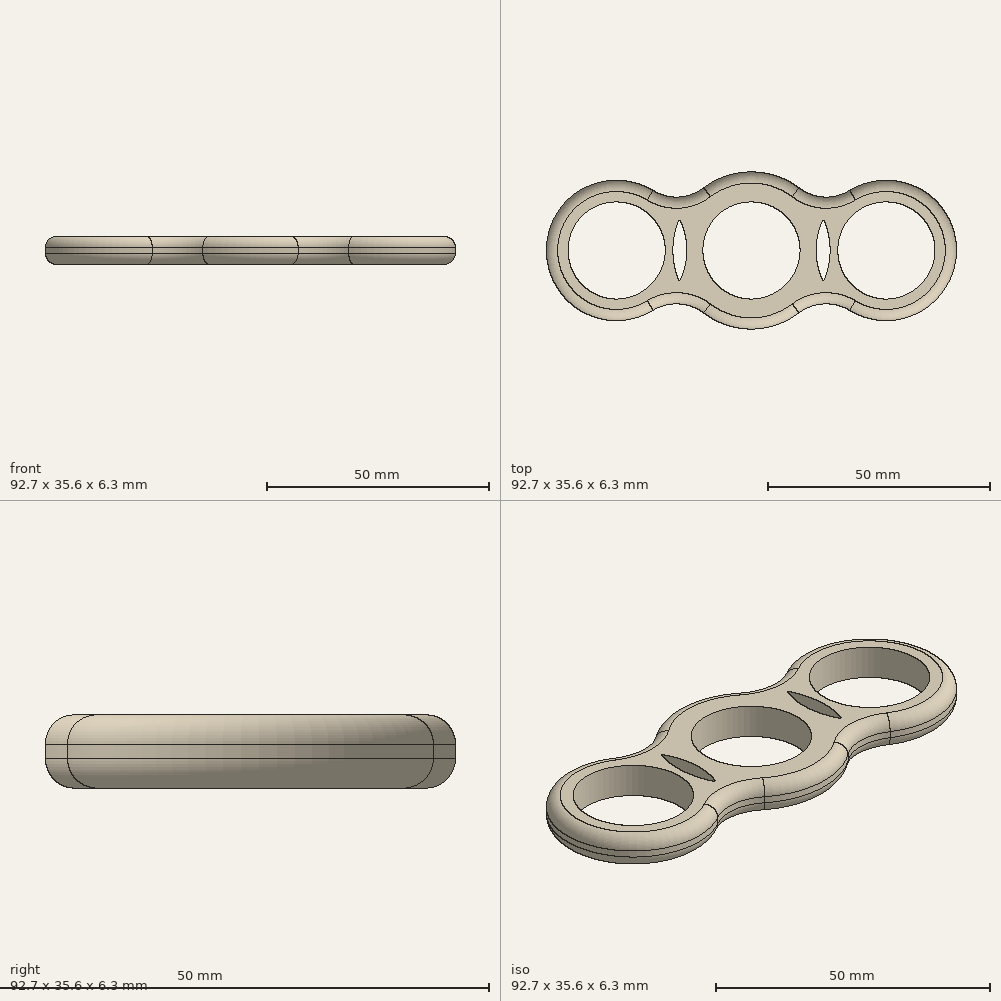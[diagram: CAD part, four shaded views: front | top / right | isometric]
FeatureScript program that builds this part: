
annotation { "Feature Type Name" : "Feature", "Feature Type Description" : "" }
export const myFeature = defineFeature(function(context is Context, id is Id, definition is map)
    precondition{}
    {
        {
            var Q0;
            Q0=qCreatedBy(makeId("Top.planeOp"),FACE);
            var sketch = newSketch(context, id + "F0", { "sketchPlane" : qUnion([Q0])});
            skCircle(sketch, "E0", {"center": v(0, 0) * mm, "radius": 10.99 * mm});
            skLineSegment(sketch, "E1", {"start": v(0, 0) * mm, "end": v(30.48, 0) * mm});
            skLineSegment(sketch, "E2", {"start": v(0, 0) * mm, "end": v(-30.48, 0) * mm});
            skCircle(sketch, "E3", {"center": v(-30.48, 0) * mm, "radius": 10.99 * mm});
            skCircle(sketch, "E4", {"center": v(30.48, 0) * mm, "radius": 10.99 * mm});
            skCircle(sketch, "E5", {"center": v(-30.48, 0) * mm, "radius": 15.88 * mm});
            skCircle(sketch, "E6", {"center": v(30.48, 0) * mm, "radius": 15.88 * mm});
            skCircle(sketch, "E7", {"center": v(0, 0) * mm, "radius": 17.78 * mm});
            skArc(sketch, "E8", {"start": v(-22.22, 13.55) * mm, "mid": v(-16.4, 12.08) * mm, "end": v(-10.77, 14.15) * mm});
            skArc(sketch, "E9", {"start": v(-10.77, -14.15) * mm, "mid": v(-16.4, -12.08) * mm, "end": v(-22.22, -13.55) * mm});
            skArc(sketch, "E10", {"start": v(10.77, 14.15) * mm, "mid": v(16.4, 12.08) * mm, "end": v(22.22, 13.55) * mm});
            skArc(sketch, "E11", {"start": v(22.22, -13.55) * mm, "mid": v(16.4, -12.08) * mm, "end": v(10.77, -14.15) * mm});
            skSolve(sketch);
        }
        {
            var Q0;
            Q0=makeQuery(id+"F0.imprint","IMPRINT",FACE,{"disambiguationData":[TD([[makeQuery(id+"F0.imprint","IMPRINT",EDGE,{"derivedFrom":sQuery(id+"F0.wireOp",EDGE,"E3")}),-1.0]])]});
            var Q1;
            {var subQ0=sQuery(id+"F0.wireOp",EDGE,"E8");Q1=makeQuery(id+"F0.imprint","IMPRINT",FACE,{"disambiguationData":[TD([[makeQuery(id+"F0.imprint","IMPRINT",EDGE,{"derivedFrom":subQ0}),-1.0]])]});}
            var Q2;
            {var subQ0=sQuery(id+"F0.wireOp",EDGE,"E9");Q2=makeQuery(id+"F0.imprint","IMPRINT",FACE,{"disambiguationData":[TD([[makeQuery(id+"F0.imprint","IMPRINT",EDGE,{"derivedFrom":subQ0}),-1.0]])]});}
            var Q3;
            {var subQ5=sQuery(id+"F0.wireOp",EDGE,"E1");var subQ6=sQuery(id+"F0.wireOp",EDGE,"E0");var subQ7=makeQuery(id+"F0.imprint","INTERSECT",VERTEX,{"derivedFrom":[subQ6,subQ5]});Q3=makeQuery(id+"F0.imprint","IMPRINT",FACE,{"disambiguationData":[TD([[makeQuery(id+"F0.imprint","IMPRINT",EDGE,{"disambiguationData":[TD([[subQ7,1.0]])],"derivedFrom":subQ6}),-1.0]])]});}
            var Q4;
            {var subQ5=sQuery(id+"F0.wireOp",EDGE,"E1");var subQ6=sQuery(id+"F0.wireOp",EDGE,"E0");var subQ7=makeQuery(id+"F0.imprint","INTERSECT",VERTEX,{"derivedFrom":[subQ6,subQ5]});Q4=makeQuery(id+"F0.imprint","IMPRINT",FACE,{"disambiguationData":[TD([[makeQuery(id+"F0.imprint","IMPRINT",EDGE,{"disambiguationData":[TD([[subQ7,-1.0]])],"derivedFrom":subQ6}),-1.0]])]});}
            var Q5;
            {var subQ0=sQuery(id+"F0.wireOp",EDGE,"E10");var subQ1=sQuery(id+"F0.wireOp",EDGE,"E6");var subQ2=makeQuery(id+"F0.imprint","INTERSECT",VERTEX,{"derivedFrom":[subQ1,subQ0]});Q5=makeQuery(id+"F0.imprint","IMPRINT",FACE,{"disambiguationData":[TD([[makeQuery(id+"F0.imprint","IMPRINT",EDGE,{"disambiguationData":[TD([[subQ2,-1.0]])],"derivedFrom":subQ1}),-1.0]])]});}
            var Q6;
            {var subQ0=sQuery(id+"F0.wireOp",EDGE,"E11");Q6=makeQuery(id+"F0.imprint","IMPRINT",FACE,{"disambiguationData":[TD([[makeQuery(id+"F0.imprint","IMPRINT",EDGE,{"derivedFrom":subQ0}),-1.0]])]});}
            var Q7;
            Q7=makeQuery(id+"F0.imprint","IMPRINT",FACE,{"disambiguationData":[TD([[makeQuery(id+"F0.imprint","IMPRINT",EDGE,{"derivedFrom":sQuery(id+"F0.wireOp",EDGE,"E4")}),-1.0]])]});
            extrude(context, id + "F1", {"entities" : qUnion([Q0, Q1, Q2, Q3, Q4, Q5, Q6, Q7]), "depth" : 6.35 * mm, "offsetDistance" : 25.4 * mm});
        }
        {
            var Q0;
            {var subQ0=sQuery(id+"F0.wireOp",EDGE,"E5");Q0=makeQuery(id+"F1.opExtrude","CAP_EDGE",EDGE,{"disambiguationData":[OSD([subQ0]),TDD([makeQuery(id+"F0.imprint","IMPRINT",EDGE,{"disambiguationData":[TD([[makeQuery(id+"F0.imprint","INTERSECT",VERTEX,{"derivedFrom":[subQ0,sQuery(id+"F0.wireOp",EDGE,"E8")]}),-1.0]])],"derivedFrom":subQ0})])],"isStart":false});}
            var Q1;
            Q1=makeQuery(id+"F1.opExtrude","CAP_EDGE",EDGE,{"disambiguationData":[OSD([sQuery(id+"F0.wireOp",EDGE,"E8")])],"isStart":false});
            var Q2;
            {var subQ0=sQuery(id+"F0.wireOp",EDGE,"E7");Q2=makeQuery(id+"F1.opExtrude","CAP_EDGE",EDGE,{"disambiguationData":[OSD([subQ0]),TDD([makeQuery(id+"F0.imprint","IMPRINT",EDGE,{"disambiguationData":[TD([[makeQuery(id+"F0.imprint","INTERSECT",VERTEX,{"derivedFrom":[subQ0,sQuery(id+"F0.wireOp",EDGE,"E8")]}),1.0]])],"derivedFrom":subQ0})])],"isStart":false});}
            var Q3;
            Q3=makeQuery(id+"F1.opExtrude","CAP_EDGE",EDGE,{"disambiguationData":[OSD([sQuery(id+"F0.wireOp",EDGE,"E10")])],"isStart":false});
            var Q4;
            {var subQ0=sQuery(id+"F0.wireOp",EDGE,"E6");Q4=makeQuery(id+"F1.opExtrude","CAP_EDGE",EDGE,{"disambiguationData":[OSD([subQ0]),TDD([makeQuery(id+"F0.imprint","IMPRINT",EDGE,{"disambiguationData":[TD([[makeQuery(id+"F0.imprint","INTERSECT",VERTEX,{"derivedFrom":[subQ0,sQuery(id+"F0.wireOp",EDGE,"E10")]}),1.0]])],"derivedFrom":subQ0})])],"isStart":false});}
            var Q5;
            Q5=makeQuery(id+"F1.opExtrude","CAP_EDGE",EDGE,{"disambiguationData":[OSD([sQuery(id+"F0.wireOp",EDGE,"E11")])],"isStart":false});
            var Q6;
            {var subQ0=sQuery(id+"F0.wireOp",EDGE,"E7");Q6=makeQuery(id+"F1.opExtrude","CAP_EDGE",EDGE,{"disambiguationData":[OSD([subQ0]),TDD([makeQuery(id+"F0.imprint","IMPRINT",EDGE,{"disambiguationData":[TD([[makeQuery(id+"F0.imprint","INTERSECT",VERTEX,{"derivedFrom":[subQ0,sQuery(id+"F0.wireOp",EDGE,"E9")]}),-1.0]])],"derivedFrom":subQ0})])],"isStart":false});}
            var Q7;
            Q7=makeQuery(id+"F1.opExtrude","CAP_EDGE",EDGE,{"disambiguationData":[OSD([sQuery(id+"F0.wireOp",EDGE,"E9")])],"isStart":false});
            var Q8;
            {var subQ0=sQuery(id+"F0.wireOp",EDGE,"E5");Q8=makeQuery(id+"F1.opExtrude","CAP_EDGE",EDGE,{"disambiguationData":[OSD([subQ0]),TDD([makeQuery(id+"F0.imprint","IMPRINT",EDGE,{"disambiguationData":[TD([[makeQuery(id+"F0.imprint","INTERSECT",VERTEX,{"derivedFrom":[subQ0,sQuery(id+"F0.wireOp",EDGE,"E8")]}),-1.0]])],"derivedFrom":subQ0})])],"isStart":true});}
            var Q9;
            Q9=makeQuery(id+"F1.opExtrude","CAP_EDGE",EDGE,{"disambiguationData":[OSD([sQuery(id+"F0.wireOp",EDGE,"E9")])],"isStart":true});
            var Q10;
            {var subQ0=sQuery(id+"F0.wireOp",EDGE,"E7");Q10=makeQuery(id+"F1.opExtrude","CAP_EDGE",EDGE,{"disambiguationData":[OSD([subQ0]),TDD([makeQuery(id+"F0.imprint","IMPRINT",EDGE,{"disambiguationData":[TD([[makeQuery(id+"F0.imprint","INTERSECT",VERTEX,{"derivedFrom":[subQ0,sQuery(id+"F0.wireOp",EDGE,"E9")]}),-1.0]])],"derivedFrom":subQ0})])],"isStart":true});}
            var Q11;
            Q11=makeQuery(id+"F1.opExtrude","CAP_EDGE",EDGE,{"disambiguationData":[OSD([sQuery(id+"F0.wireOp",EDGE,"E8")])],"isStart":true});
            var Q12;
            {var subQ0=sQuery(id+"F0.wireOp",EDGE,"E7");Q12=makeQuery(id+"F1.opExtrude","CAP_EDGE",EDGE,{"disambiguationData":[OSD([subQ0]),TDD([makeQuery(id+"F0.imprint","IMPRINT",EDGE,{"disambiguationData":[TD([[makeQuery(id+"F0.imprint","INTERSECT",VERTEX,{"derivedFrom":[subQ0,sQuery(id+"F0.wireOp",EDGE,"E8")]}),1.0]])],"derivedFrom":subQ0})])],"isStart":true});}
            var Q13;
            Q13=makeQuery(id+"F1.opExtrude","CAP_EDGE",EDGE,{"disambiguationData":[OSD([sQuery(id+"F0.wireOp",EDGE,"E11")])],"isStart":true});
            var Q14;
            {var subQ0=sQuery(id+"F0.wireOp",EDGE,"E6");Q14=makeQuery(id+"F1.opExtrude","CAP_EDGE",EDGE,{"disambiguationData":[OSD([subQ0]),TDD([makeQuery(id+"F0.imprint","IMPRINT",EDGE,{"disambiguationData":[TD([[makeQuery(id+"F0.imprint","INTERSECT",VERTEX,{"derivedFrom":[subQ0,sQuery(id+"F0.wireOp",EDGE,"E10")]}),1.0]])],"derivedFrom":subQ0})])],"isStart":true});}
            var Q15;
            Q15=makeQuery(id+"F1.opExtrude","CAP_EDGE",EDGE,{"disambiguationData":[OSD([sQuery(id+"F0.wireOp",EDGE,"E10")])],"isStart":true});
            fillet(context, id + "F2", {"entities" : qUnion([Q0, Q1, Q2, Q3, Q4, Q5, Q6, Q7, Q8, Q9, Q10, Q11, Q12, Q13, Q14, Q15]), "radius" : 2.54 * mm, "tangentPropagation" : true, "allowEdgeOverflow" : false});
        }
    });
